# Revit family: Differenzdruckregler F_4007_50-150kPa
name_source: partatom
category: Rohrzubehör
units: mm (PartAtom-declared; Revit-internal decimal feet)

## family parameters
Arbeitsebenenbasiert = Nein
Beim Laden mit Abzugskörper schneiden = Nein
Bemaßung runder Anschluss = Durchmesser verwenden
Gemeinsam genutzt = Nein
Immer vertikal = Ja
OmniClass-Nummer = 23.65.55.14
OmniClass-Titel = Valves for Liquid Services
Teiletyp = Unterbricht

## types (1)
- Differenzdruckregler F_4007_50-150kPa
    Anschlussflansch = EN 1092-2
    Anwendung = Für Heizungs- und Kühlanlagen um den Differenzdruck innerhalb des regeltechnischen Bereiches konstant zu halten.
    Ausführung = Der Differenzdruckregler ist ein Proportionalregler in Geradsitzausführung und arbeitet ohne Hilfsenergie für Zweirohranlagen. Der gewünschte Differenzdruck- Sollwert kann zwischen 50 und 150 kPa stufenlos eingestellt werden.
    D03 = 21 mm  [stored 0.0688976 ft]
    D07 = 30 mm  [stored 0.0984252 ft]
    D08 = 24 mm  [stored 0.0787402 ft]
    D14 = 50 mm  [stored 0.164042 ft]
    D15 = 35 mm  [stored 0.114829 ft]
    D16 = 45 mm  [stored 0.147638 ft]
    D17 = 6 mm  [stored 0.019685 ft]
    Differenzdruck Einstellbereich = 50-150 kPa
    Gehäuse = Grauguss GJL250 nach EN 1561
    H04 = 5 mm  [stored 0.0164042 ft]
    H05 = 3 mm  [stored 0.00984252 ft]
    H08 = 21 mm  [stored 0.0688976 ft]
    H10 = 5 mm  [stored 0.0164042 ft]
    H13 = 17 mm  [stored 0.0557743 ft]
    H14 = 5 mm  [stored 0.0164042 ft]
    H15 = 25 mm  [stored 0.082021 ft]
    H16 = 10 mm  [stored 0.0328084 ft]
    H17 = 6 mm  [stored 0.019685 ft]
    Hersteller = HERZ Armaturen Ges.m.b.H.
    L01 = 3 mm  [stored 0.00984252 ft]
    L03 = 10 mm  [stored 0.0328084 ft]
    Max. Betriebsdruck = 1600000.0 Pa
    Max. Betriebstemperatur = 110 °C
    Medium = Die Verwendung von Ethylen- und Propylenglykol ist im Mischungsverhältnis 25 - 50 % zulässig. Heizwasserqualität entsprechend ÖNORM H 5195 bzw. VDI-Richtlinie 2035
    Membrane und O-Ringe = EPDM
    Min. Betriebstemperatur = 2 °C
    Min. Betriebstemperatur (Frostschutz) = -10 °C
    R02 = 16 mm  [stored 0.0524934 ft]
    R97 = 2 mm  [stored 0.00656168 ft]
    R98 = 6 mm  [stored 0.019685 ft]
    R99 = 14 mm  [stored 0.0459318 ft]
    SCRNCODE = 05;03;02
    SCRNSEQ = ARM;ARM_TYP="DIFR";2
    Sollwertfeder = EN 10270-1-SH
    URL = www.herz-armaturen.at

note: [stored X ft] marks values corroborated as IEEE doubles in the binary element streams (Revit-internal decimal feet)
